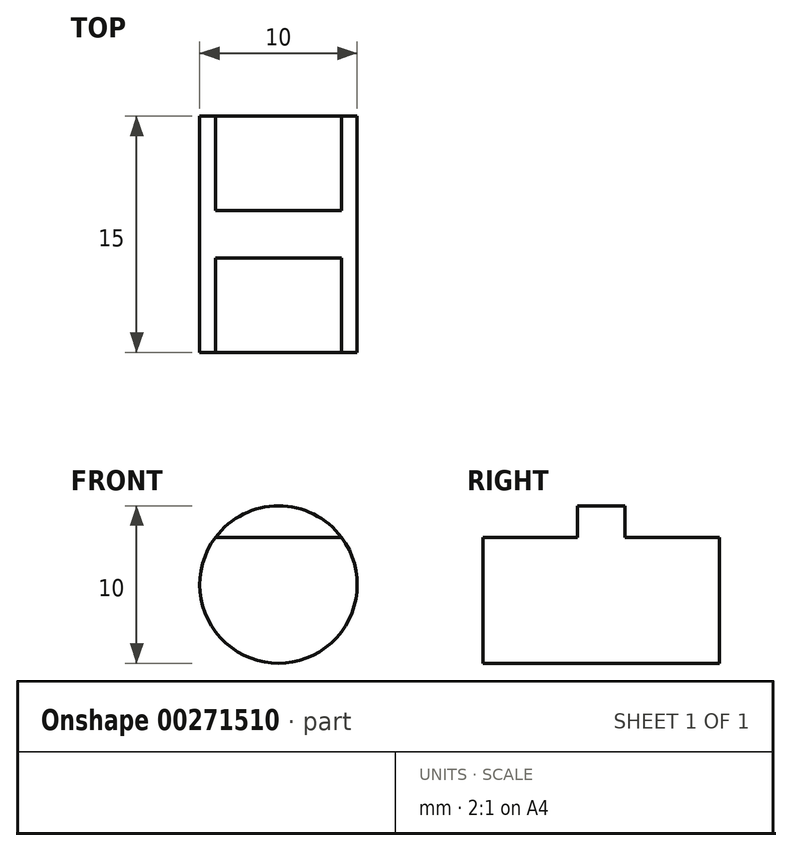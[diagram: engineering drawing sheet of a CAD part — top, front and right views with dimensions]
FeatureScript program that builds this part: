
annotation { "Feature Type Name" : "Feature", "Feature Type Description" : "" }
export const myFeature = defineFeature(function(context is Context, id is Id, definition is map)
    precondition{}
    {
        {
            var Q0;
            Q0=qCreatedBy(makeId("Front.planeOp"),FACE);
            var sketch = newSketch(context, id + "F0", { "sketchPlane" : qUnion([Q0])});
            skCircle(sketch, "E0", {"center": v(0, 0) * mm, "radius": 5 * mm});
            skSolve(sketch);
        }
        {
            var Q0;
            Q0=makeQuery(id+"F0.imprint","IMPRINT",FACE,{"disambiguationData":[TD([[makeQuery(id+"F0.imprint","IMPRINT",EDGE,{"derivedFrom":sQuery(id+"F0.wireOp",EDGE,"E0")}),1.0]])]});
            extrude(context, id + "F1", {"entities" : qUnion([Q0]), "depth" : 15 * mm});
        }
        {
            var Q0;
            Q0=makeQuery(id+"F1.opExtrude","CAP_FACE",FACE,{"disambiguationData":[OSD([sQuery(id+"F0.wireOp",EDGE,"E0")])],"isStart":false});
            var sketch = newSketch(context, id + "F2", { "sketchPlane" : qUnion([Q0])});
            skLineSegment(sketch, "E1", {"start": v(-4, 3) * mm, "end": v(4, 3) * mm});
            skArc(sketch, "E2", {"start": v(-4, 3) * mm, "mid": v(0, 5) * mm, "end": v(4, 3) * mm});
            skSolve(sketch);
        }
        {
            var Q0;
            Q0=makeQuery(id+"F2.imprint","IMPRINT",FACE,{"disambiguationData":[TD([[makeQuery(id+"F2.imprint","IMPRINT",EDGE,{"derivedFrom":sQuery(id+"F2.wireOp",EDGE,"E1")}),1.0]])]});
            extrude(context, id + "F3", {"entities" : qUnion([Q0]), "operationType" : NewBodyOperationType.REMOVE, "oppositeDirection" : true, "depth" : 6 * mm});
        }
        {
            var Q0;
            Q0=makeQuery(id+"F1.opExtrude","CAP_FACE",FACE,{"disambiguationData":[OSD([sQuery(id+"F0.wireOp",EDGE,"E0")])],"isStart":true});
            var sketch = newSketch(context, id + "F4", { "sketchPlane" : qUnion([Q0])});
            skLineSegment(sketch, "E3", {"start": v(-4, 3) * mm, "end": v(4, 3) * mm});
            skArc(sketch, "E4", {"start": v(-4, 3) * mm, "mid": v(0, 5) * mm, "end": v(4, 3) * mm});
            skSolve(sketch);
        }
        {
            var Q0;
            Q0=makeQuery(id+"F4.imprint","IMPRINT",FACE,{"disambiguationData":[TD([[makeQuery(id+"F4.imprint","IMPRINT",EDGE,{"derivedFrom":sQuery(id+"F4.wireOp",EDGE,"E3")}),1.0]])]});
            extrude(context, id + "F5", {"entities" : qUnion([Q0]), "operationType" : NewBodyOperationType.REMOVE, "oppositeDirection" : true, "depth" : 6 * mm});
        }
    });
